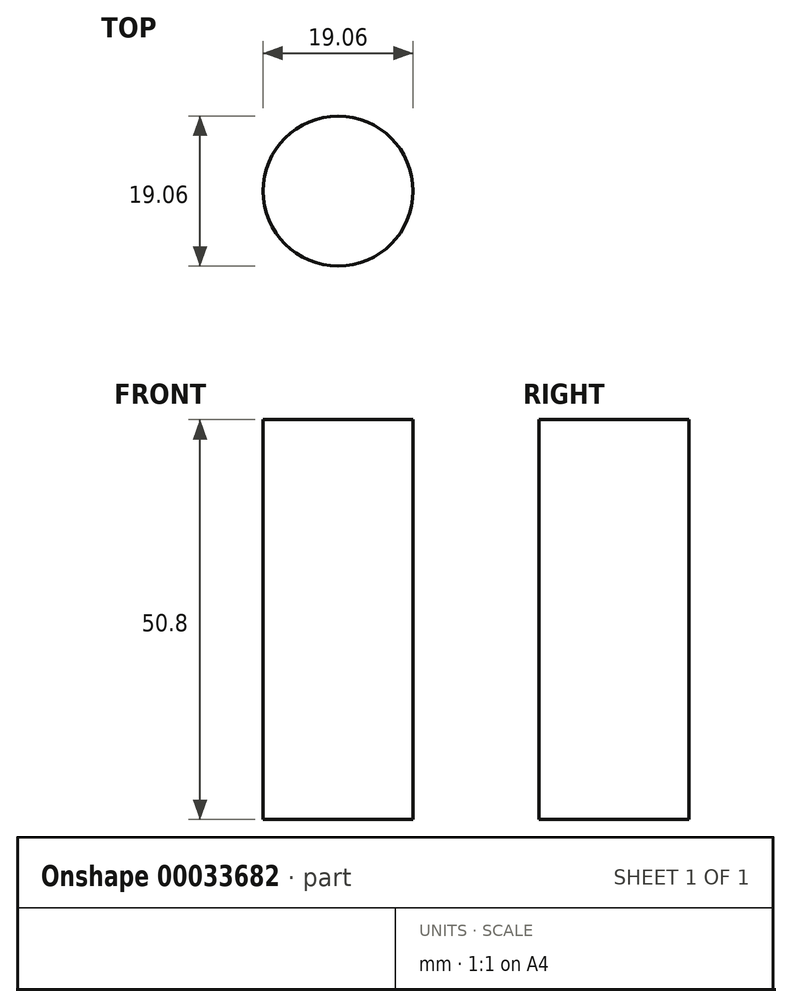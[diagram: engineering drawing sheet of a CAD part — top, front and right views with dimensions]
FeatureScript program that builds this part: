
annotation { "Feature Type Name" : "Feature", "Feature Type Description" : "" }
export const myFeature = defineFeature(function(context is Context, id is Id, definition is map)
    precondition{}
    {
        {
            var Q0;
            Q0=qCreatedBy(makeId("Front.planeOp"),FACE);
            var sketch = newSketch(context, id + "F0", { "sketchPlane" : qUnion([Q0])});
            skLineSegment(sketch, "E0", {"start": v(0, 37.9) * mm, "end": v(0, -27.9) * mm});
            skLineSegment(sketch, "E1", {"start": v(0, -27.9) * mm, "end": v(0, 37.9) * mm, "construction": true});
            skLineSegment(sketch, "E2.bottom", {"start": v(0, 28.22) * mm, "end": v(9.53, 28.22) * mm});
            skLineSegment(sketch, "E2.top", {"start": v(0, -22.58) * mm, "end": v(9.53, -22.58) * mm});
            skLineSegment(sketch, "E2.left", {"start": v(0, 28.22) * mm, "end": v(0, -22.58) * mm});
            skLineSegment(sketch, "E2.right", {"start": v(9.53, 28.22) * mm, "end": v(9.53, -22.58) * mm});
            skSolve(sketch);
        }
        {
            var Q0;
            Q0 = qSketchRegion(id + "F0", true);
            var Q1;
            Q1=sQuery(id+"F0.wireOp",EDGE,"E2.left");
            revolve(context, id + "F1", {"entities" : qUnion([Q0]), "axis" : qUnion([Q1]), "revolveType" : RevolveType.FULL});
        }
    });
